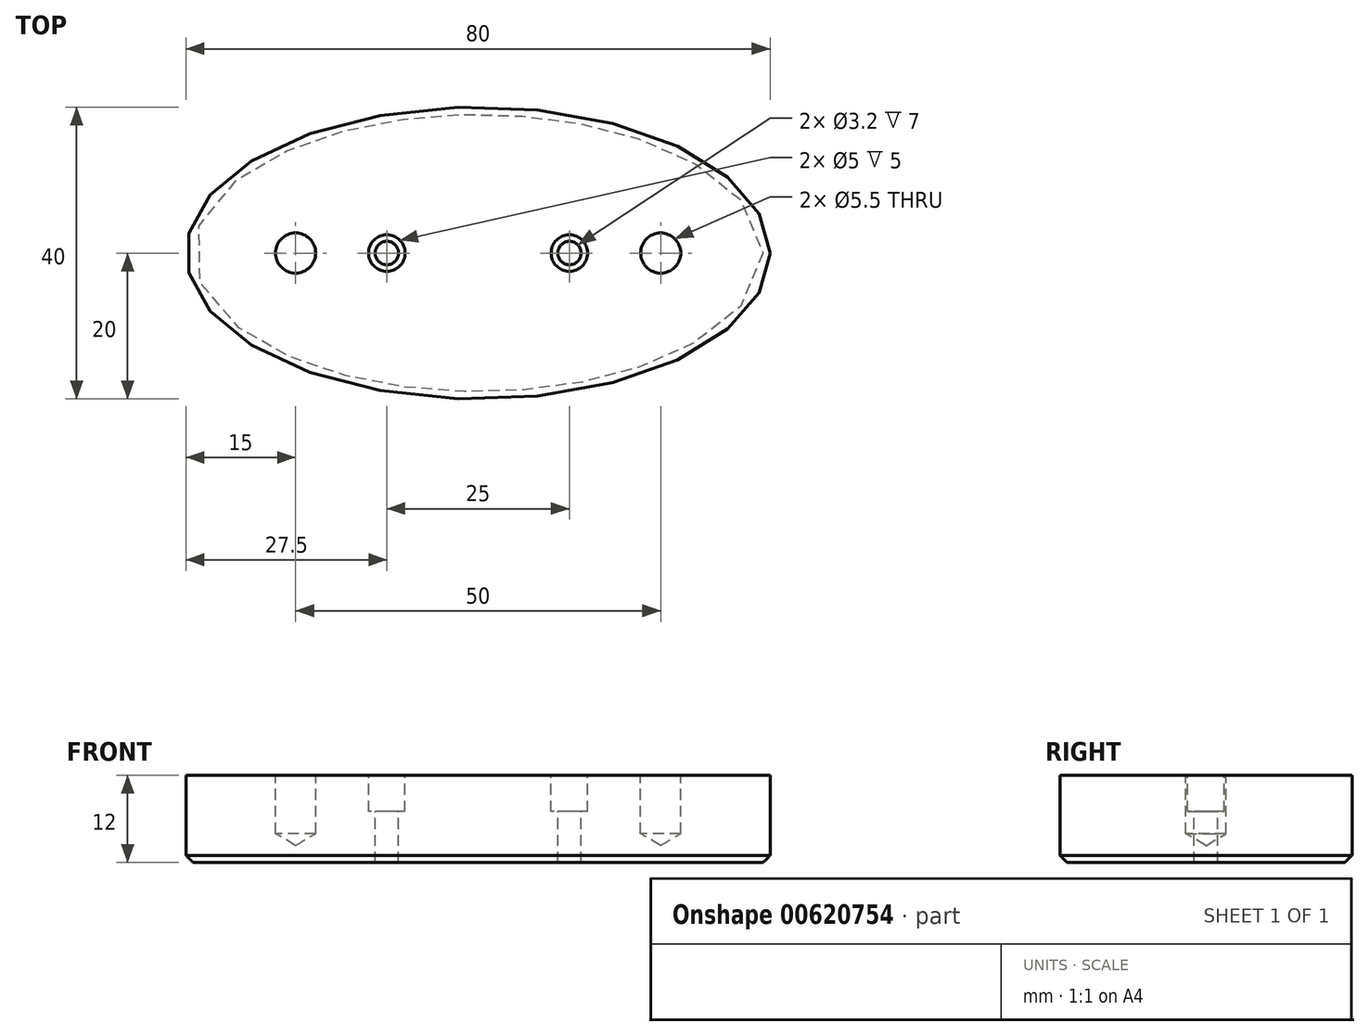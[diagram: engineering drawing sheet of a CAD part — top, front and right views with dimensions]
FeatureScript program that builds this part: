
annotation { "Feature Type Name" : "Feature", "Feature Type Description" : "" }
export const myFeature = defineFeature(function(context is Context, id is Id, definition is map)
    precondition{}
    {
        {
            var Q0;
            Q0=qCreatedBy(makeId("Top.planeOp"),FACE);
            var sketch = newSketch(context, id + "F0", { "sketchPlane" : qUnion([Q0])});
            skEllipse(sketch, "E0", {"center": v(-361, 0) * mm, "majorRadius": 40 * mm, "minorRadius": 20 * mm, "majorAxis": v(1, 0)});
            skSolve(sketch);
        }
        {
            var Q0;
            Q0=makeQuery(id+"F0.imprint","IMPRINT",FACE,{"disambiguationData":[TD([[makeQuery(id+"F0.imprint","IMPRINT",EDGE,{"derivedFrom":sQuery(id+"F0.wireOp",EDGE,"E0")}),1.0]])]});
            extrude(context, id + "F1", {"entities" : qUnion([Q0]), "depth" : 12 * mm, "offsetDistance" : 25 * mm});
        }
        {
            var Q0;
            Q0=makeQuery(id+"F1.opExtrude","CAP_FACE",FACE,{"disambiguationData":[OSD([sQuery(id+"F0.wireOp",EDGE,"E0")])],"isStart":false});
            var sketch = newSketch(context, id + "F2", { "sketchPlane" : qUnion([Q0])});
            skLineSegment(sketch, "E1", {"start": v(-361, 0) * mm, "end": v(-348.5, 0) * mm});
            skLineSegment(sketch, "E2", {"start": v(-361, 0) * mm, "end": v(-373.5, 0) * mm});
            skSolve(sketch);
        }
        {
            var Q0;
            Q0=sQuery(id+"F2.wireOp",VERTEX,"E2.end");
            var Q1;
            Q1=sQuery(id+"F2.wireOp",VERTEX,"E1.end");
            var Q2;
            Q2=makeQuery(id+"F1.opExtrude","SWEPT_BODY",BODY,{"disambiguationData":[OSD([sQuery(id+"F0.wireOp",EDGE,"E0")])]});
            hole(context, id + "F3", {"style" : HoleStyle.C_BORE, "endStyle" : HoleEndStyle.THROUGH, "holeDiameter" : 3.2 * mm, "cBoreDiameter" : 5 * mm, "cBoreDepth" : 5 * mm, "majorDiameter" : 5 * mm, "isTappedThrough" : true, "tappedDepth" : 12 * mm, "tapClearance" : 3, "locations" : qUnion([Q0, Q1]), "scope" : qUnion([Q2])});
        }
        {
            var Q0;
            Q0=makeQuery(id+"F1.opExtrude","CAP_FACE",FACE,{"disambiguationData":[OSD([sQuery(id+"F0.wireOp",EDGE,"E0")])],"isStart":false});
            var sketch = newSketch(context, id + "F4", { "sketchPlane" : qUnion([Q0])});
            skLineSegment(sketch, "E3", {"start": v(-361, 0) * mm, "end": v(-386, 0) * mm});
            skLineSegment(sketch, "E4", {"start": v(-361, 0) * mm, "end": v(-336, 0) * mm});
            skSolve(sketch);
        }
        {
            var Q0;
            Q0=sQuery(id+"F4.wireOp",VERTEX,"E3.end");
            var Q1;
            Q1=sQuery(id+"F4.wireOp",VERTEX,"E4.end");
            var Q2;
            Q2=makeQuery(id+"F1.opExtrude","SWEPT_BODY",BODY,{"disambiguationData":[OSD([sQuery(id+"F0.wireOp",EDGE,"E0")])]});
            hole(context, id + "F5", {"style" : HoleStyle.SIMPLE, "endStyle" : HoleEndStyle.BLIND, "standardTappedOrClearance" : lookupTablePath({ "standard" : "ISO", "fit" : "Normal", "size" : "M5", "type" : "Clearance" }), "standardBlindInLast" : lookupTablePath({ "fit" : "Standard", "standard" : "ISO", "size" : "M5", "type" : "Clearance" }), "holeDiameter" : 5.5 * mm, "majorDiameter" : 5 * mm, "holeDepth" : 8 * mm, "isTappedThrough" : true, "tappedDepth" : 12 * mm, "tapClearance" : 3, "locations" : qUnion([Q0, Q1]), "scope" : qUnion([Q2])});
        }
        {
            var Q0;
            Q0=makeQuery(id+"F1.opExtrude","CAP_EDGE",EDGE,{"disambiguationData":[OSD([sQuery(id+"F0.wireOp",EDGE,"E0")])],"isStart":true});
            chamfer(context, id + "F6", {"entities" : qUnion([Q0]), "width" : 1 * mm, "tangentPropagation" : true});
        }
    });
